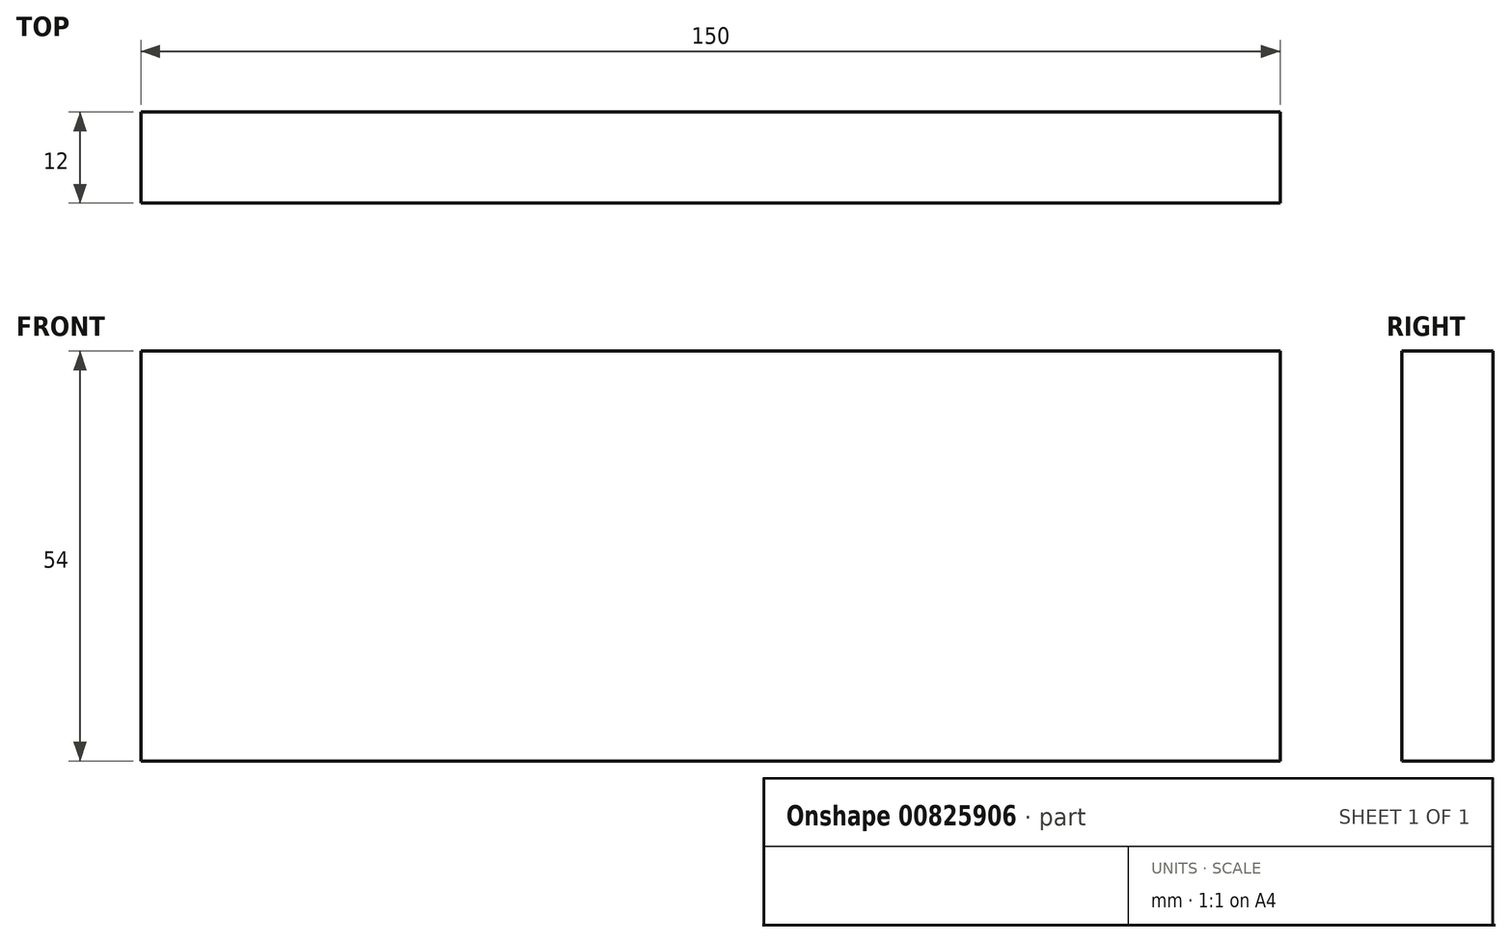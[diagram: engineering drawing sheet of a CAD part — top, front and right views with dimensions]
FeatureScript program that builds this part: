
annotation { "Feature Type Name" : "Feature", "Feature Type Description" : "" }
export const myFeature = defineFeature(function(context is Context, id is Id, definition is map)
    precondition{}
    {
        {
            var Q0;
            Q0=qCreatedBy(makeId("Right.planeOp"),FACE);
            var sketch = newSketch(context, id + "F0", { "sketchPlane" : qUnion([Q0])});
            skLineSegment(sketch, "E0.bottom", {"start": v(0, 0) * mm, "end": v(12, 0) * mm});
            skLineSegment(sketch, "E0.top", {"start": v(0, 54) * mm, "end": v(12, 54) * mm});
            skLineSegment(sketch, "E0.left", {"start": v(0, 0) * mm, "end": v(0, 54) * mm});
            skLineSegment(sketch, "E0.right", {"start": v(12, 0) * mm, "end": v(12, 54) * mm});
            skSolve(sketch);
        }
        {
            var Q0;
            Q0=makeQuery(id+"F0.imprint","IMPRINT",FACE,{"disambiguationData":[TD([[makeQuery(id+"F0.imprint","IMPRINT",EDGE,{"derivedFrom":sQuery(id+"F0.wireOp",EDGE,"E0.bottom")}),1.0]])]});
            extrude(context, id + "F1", {"entities" : qUnion([Q0]), "depth" : 150 * mm, "offsetDistance" : 25 * mm});
        }
    });
